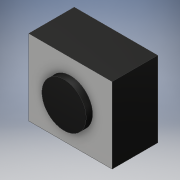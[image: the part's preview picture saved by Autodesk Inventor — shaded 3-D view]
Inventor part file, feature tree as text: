
AUTODESK INVENTOR PART (.ipt)
format: ipt  version: 2017 (Build 210142000, 142)  size: 106,496 bytes
history: native  units: in
note: dims shown in document units (in); Inventor stores cm internally (conversion verified against a paired STEP export)
features: extrude x2, sketch x2, projected_geometry x1
ambient origin geometry x8: Origin, YZ Plane, XZ Plane, XY Plane, X Axis, Y Axis, Z Axis, Center Point
bodies: Solid1 (feature_tree)
feature tree (5):
  extrude  "Extrusion1"  Depth=0.26in
  extrude  "Extrusion2"  Depth=0.02in
  sketch  "Sketch1"  dims[d0=0.236in d1=0.26in]
  sketch  "Sketch2"  dims[d2=0.142in d3=0.0in d4=0.138in d5=0.02in d6=0.0in]
  projected_geometry  "Projected Loop1"
